annotation { "Feature Type Name" : "Feature", "Feature Type Description" : "" }
export const myFeature = defineFeature(function(context is Context, id is Id, definition is map)
    precondition{}
    {
        {
            var Q0;
            Q0=qCreatedBy(makeId("Front.planeOp"),FACE);
            var sketch = newSketch(context, id + "F0", { "sketchPlane" : qUnion([Q0])});
            skLineSegment(sketch, "E0.bottom", {"start": v(0, 0) * mm, "end": v(213.75, 0) * mm});
            skLineSegment(sketch, "E0.top", {"start": v(0, 261.75) * mm, "end": v(213.75, 261.75) * mm});
            skLineSegment(sketch, "E0.left", {"start": v(0, 0) * mm, "end": v(0, 261.75) * mm});
            skLineSegment(sketch, "E0.right", {"start": v(213.75, 0) * mm, "end": v(213.75, 261.75) * mm});
            skSolve(sketch);
        }
        {
            var Q0;
            Q0 = qSketchRegion(id + "F0", true);
            extrude(context, id + "F1", {"entities" : qUnion([Q0]), "oppositeDirection" : true, "depth" : 2 * mm, "offsetDistance" : 25 * mm});
        }
        {
            var Q0;
            Q0=qCreatedBy(makeId("Front.planeOp"),FACE);
            var sketch = newSketch(context, id + "F2", { "sketchPlane" : qUnion([Q0])});
            skCircle(sketch, "E1", {"center": v(41.2, 23.32) * mm, "radius": 8 * mm});
            skSolve(sketch);
        }
        {
            var Q0;
            Q0 = qSketchRegion(id + "F2", true);
            extrude(context, id + "F3", {"entities" : qUnion([Q0]), "operationType" : NewBodyOperationType.REMOVE, "oppositeDirection" : true, "depth" : 25 * mm, "offsetDistance" : 25 * mm});
        }
        {
            var Q0;
            Q0=makeQuery(id+"F1.opExtrude","CAP_FACE",FACE,{"disambiguationData":[OSD([sQuery(id+"F0.wireOp",EDGE,"E0.bottom"),sQuery(id+"F0.wireOp",EDGE,"E0.top"),sQuery(id+"F0.wireOp",EDGE,"E0.left"),sQuery(id+"F0.wireOp",EDGE,"E0.right")])],"isStart":true});
            var sketch = newSketch(context, id + "F4", { "sketchPlane" : qUnion([Q0])});
            skLineSegment(sketch, "E2.bottom", {"start": v(151.6, 32.62) * mm, "end": v(138.6, 32.62) * mm});
            skLineSegment(sketch, "E2.top", {"start": v(151.6, 14.02) * mm, "end": v(138.6, 14.02) * mm});
            skLineSegment(sketch, "E2.left", {"start": v(151.6, 32.62) * mm, "end": v(151.6, 14.02) * mm});
            skLineSegment(sketch, "E2.right", {"start": v(138.6, 32.62) * mm, "end": v(138.6, 14.02) * mm});
            skPoint(sketch, "E2.middle", {"position": v(145.1, 23.32) * mm});
            skSolve(sketch);
        }
        {
            var Q0;
            Q0 = qSketchRegion(id + "F4", true);
            extrude(context, id + "F5", {"entities" : qUnion([Q0]), "operationType" : NewBodyOperationType.REMOVE, "oppositeDirection" : true, "depth" : 25 * mm, "offsetDistance" : 25 * mm});
        }
        {
            var Q0;
            Q0=makeQuery(id+"F1.opExtrude","CAP_FACE",FACE,{"disambiguationData":[OSD([sQuery(id+"F0.wireOp",EDGE,"E0.bottom"),sQuery(id+"F0.wireOp",EDGE,"E0.top"),sQuery(id+"F0.wireOp",EDGE,"E0.left"),sQuery(id+"F0.wireOp",EDGE,"E0.right")])],"isStart":true});
            var sketch = newSketch(context, id + "F6", { "sketchPlane" : qUnion([Q0])});
            skText(sketch, "E3", { "text": "Emergency Stop", "fontName": "OpenSans-Regular.ttf"});
            const initialGuessF6  = {"E3": [0.058, 0.021, 1, 0, 0.005]};
            skSetInitialGuess(sketch, initialGuessF6);
            skSolve(sketch);
        }
        {
            var Q0;
            Q0 = qSketchRegion(id + "F6", true);
            extrude(context, id + "F7", {"entities" : qUnion([Q0]), "operationType" : NewBodyOperationType.REMOVE, "oppositeDirection" : true, "depth" : 0.5 * mm, "offsetDistance" : 25 * mm});
        }
        {
            var Q0;
            {var subQ0=sQuery(id+"F0.wireOp",EDGE,"E0.right");var subQ1=sQuery(id+"F0.wireOp",EDGE,"E0.left");var subQ2=sQuery(id+"F0.wireOp",EDGE,"E0.top");var subQ3=sQuery(id+"F0.wireOp",EDGE,"E0.bottom");Q0=makeQuery(id+"F7.boolean.opBoolean","SPLIT",FACE,{"disambiguationData":[TD([makeQuery(id+"F1.opExtrude","SWEPT_FACE",FACE,{"disambiguationData":[OSD([subQ3])]})])],"derivedFrom":makeQuery(id+"F1.opExtrude","CAP_FACE",FACE,{"disambiguationData":[OSD([subQ3,subQ2,subQ1,subQ0])],"isStart":true})});}
            var sketch = newSketch(context, id + "F8", { "sketchPlane" : qUnion([Q0])});
            skText(sketch, "E4", { "text": "Power", "fontName": "OpenSans-Bold.ttf"});
            const initialGuessF8  = {"E4": [0.157, 0.021, 1, 0, 0.00489]};
            skSetInitialGuess(sketch, initialGuessF8);
            skSolve(sketch);
        }
        {
            var Q0;
            Q0 = qSketchRegion(id + "F8", true);
            extrude(context, id + "F9", {"entities" : qUnion([Q0]), "operationType" : NewBodyOperationType.REMOVE, "oppositeDirection" : true, "depth" : 0.5 * mm, "offsetDistance" : 25 * mm});
        }
        {
            var Q0;
            {var subQ1=sQuery(id+"F0.wireOp",EDGE,"E0.bottom");var subQ2=makeQuery(id+"F1.opExtrude","SWEPT_FACE",FACE,{"disambiguationData":[OSD([subQ1])]});var subQ96=sQuery(id+"F0.wireOp",EDGE,"E0.right");var subQ100=sQuery(id+"F0.wireOp",EDGE,"E0.left");var subQ104=sQuery(id+"F0.wireOp",EDGE,"E0.top");Q0=makeQuery(id+"F9.boolean.opBoolean","SPLIT",FACE,{"disambiguationData":[TD([subQ2])],"derivedFrom":makeQuery(id+"F7.boolean.opBoolean","SPLIT",FACE,{"disambiguationData":[TD([subQ2])],"derivedFrom":makeQuery(id+"F1.opExtrude","CAP_FACE",FACE,{"disambiguationData":[OSD([subQ1,subQ104,subQ100,subQ96])],"isStart":true})})});}
            var sketch = newSketch(context, id + "F10", { "sketchPlane" : qUnion([Q0])});
            skCircle(sketch, "E5", {"center": v(41, 50) * mm, "radius": 1.35 * mm});
            skCircle(sketch, "E6", {"center": v(85, 50) * mm, "radius": 1.35 * mm});
            skCircle(sketch, "E7", {"center": v(129, 50) * mm, "radius": 1.35 * mm});
            skCircle(sketch, "E8", {"center": v(173, 50) * mm, "radius": 1.35 * mm});
            skCircle(sketch, "E9", {"center": v(41, 205.5) * mm, "radius": 1.35 * mm});
            skCircle(sketch, "E10", {"center": v(85, 205.5) * mm, "radius": 1.35 * mm});
            skCircle(sketch, "E11", {"center": v(129, 205.5) * mm, "radius": 1.35 * mm});
            skCircle(sketch, "E12", {"center": v(173, 205.5) * mm, "radius": 1.35 * mm});
            skCircle(sketch, "E13", {"center": v(11.88, 80) * mm, "radius": 1.35 * mm});
            skCircle(sketch, "E14", {"center": v(201.88, 80) * mm, "radius": 1.35 * mm});
            skCircle(sketch, "E15", {"center": v(201.88, 130) * mm, "radius": 1.35 * mm});
            skCircle(sketch, "E16", {"center": v(11.88, 130) * mm, "radius": 1.35 * mm});
            skCircle(sketch, "E17", {"center": v(11.88, 180) * mm, "radius": 1.35 * mm});
            skCircle(sketch, "E18", {"center": v(201.88, 180) * mm, "radius": 1.35 * mm});
            skSolve(sketch);
        }
        {
            var Q0;
            Q0 = qSketchRegion(id + "F10", true);
            extrude(context, id + "F11", {"entities" : qUnion([Q0]), "operationType" : NewBodyOperationType.REMOVE, "oppositeDirection" : true, "depth" : 25 * mm, "offsetDistance" : 25 * mm});
        }
        {
            var Q0;
            {var subQ1=sQuery(id+"F0.wireOp",EDGE,"E0.bottom");var subQ2=makeQuery(id+"F1.opExtrude","SWEPT_FACE",FACE,{"disambiguationData":[OSD([subQ1])]});var subQ96=sQuery(id+"F0.wireOp",EDGE,"E0.right");var subQ100=sQuery(id+"F0.wireOp",EDGE,"E0.left");var subQ104=sQuery(id+"F0.wireOp",EDGE,"E0.top");Q0=makeQuery(id+"F9.boolean.opBoolean","SPLIT",FACE,{"disambiguationData":[TD([subQ2])],"derivedFrom":makeQuery(id+"F7.boolean.opBoolean","SPLIT",FACE,{"disambiguationData":[TD([subQ2])],"derivedFrom":makeQuery(id+"F1.opExtrude","CAP_FACE",FACE,{"disambiguationData":[OSD([subQ1,subQ104,subQ100,subQ96])],"isStart":true})})});}
            var sketch = newSketch(context, id + "F12", { "sketchPlane" : qUnion([Q0])});
            skLineSegment(sketch, "E19.bottom", {"start": v(157.88, 75.5) * mm, "end": v(55.88, 75.5) * mm});
            skLineSegment(sketch, "E19.top", {"start": v(157.88, 54.5) * mm, "end": v(55.88, 54.5) * mm});
            skLineSegment(sketch, "E19.left", {"start": v(157.88, 75.5) * mm, "end": v(157.88, 54.5) * mm});
            skLineSegment(sketch, "E19.right", {"start": v(55.88, 75.5) * mm, "end": v(55.88, 54.5) * mm});
            skPoint(sketch, "E19.middle", {"position": v(106.88, 65) * mm});
            skSolve(sketch);
        }
        {
            var Q0;
            Q0 = qSketchRegion(id + "F12", true);
            extrude(context, id + "F13", {"entities" : qUnion([Q0]), "operationType" : NewBodyOperationType.REMOVE, "oppositeDirection" : true, "depth" : 25 * mm, "offsetDistance" : 25 * mm});
        }
        {
            var Q0;
            {var subQ1=sQuery(id+"F0.wireOp",EDGE,"E0.bottom");var subQ2=makeQuery(id+"F1.opExtrude","SWEPT_FACE",FACE,{"disambiguationData":[OSD([subQ1])]});var subQ96=sQuery(id+"F0.wireOp",EDGE,"E0.right");var subQ100=sQuery(id+"F0.wireOp",EDGE,"E0.left");var subQ104=sQuery(id+"F0.wireOp",EDGE,"E0.top");Q0=makeQuery(id+"F9.boolean.opBoolean","SPLIT",FACE,{"disambiguationData":[TD([subQ2])],"derivedFrom":makeQuery(id+"F7.boolean.opBoolean","SPLIT",FACE,{"disambiguationData":[TD([subQ2])],"derivedFrom":makeQuery(id+"F1.opExtrude","CAP_FACE",FACE,{"disambiguationData":[OSD([subQ1,subQ104,subQ100,subQ96])],"isStart":true})})});}
            var sketch = newSketch(context, id + "F14", { "sketchPlane" : qUnion([Q0])});
            skLineSegment(sketch, "E20.bottom", {"start": v(185.16, 186.15) * mm, "end": v(29.16, 186.15) * mm});
            skLineSegment(sketch, "E20.top", {"start": v(185.16, 98.15) * mm, "end": v(29.16, 98.15) * mm});
            skLineSegment(sketch, "E20.left", {"start": v(185.16, 186.15) * mm, "end": v(185.16, 98.15) * mm});
            skLineSegment(sketch, "E20.right", {"start": v(29.16, 186.15) * mm, "end": v(29.16, 98.15) * mm});
            skPoint(sketch, "E20.middle", {"position": v(107.16, 142.15) * mm});
            skSolve(sketch);
        }
        {
            var Q0;
            Q0 = qSketchRegion(id + "F14", true);
            extrude(context, id + "F15", {"entities" : qUnion([Q0]), "operationType" : NewBodyOperationType.REMOVE, "oppositeDirection" : true, "depth" : 25 * mm, "offsetDistance" : 25 * mm});
        }
        {
            var Q0;
            {var subQ1=sQuery(id+"F0.wireOp",EDGE,"E0.bottom");var subQ2=makeQuery(id+"F1.opExtrude","SWEPT_FACE",FACE,{"disambiguationData":[OSD([subQ1])]});var subQ96=sQuery(id+"F0.wireOp",EDGE,"E0.right");var subQ100=sQuery(id+"F0.wireOp",EDGE,"E0.left");var subQ104=sQuery(id+"F0.wireOp",EDGE,"E0.top");Q0=makeQuery(id+"F9.boolean.opBoolean","SPLIT",FACE,{"disambiguationData":[TD([subQ2])],"derivedFrom":makeQuery(id+"F7.boolean.opBoolean","SPLIT",FACE,{"disambiguationData":[TD([subQ2])],"derivedFrom":makeQuery(id+"F1.opExtrude","CAP_FACE",FACE,{"disambiguationData":[OSD([subQ1,subQ104,subQ100,subQ96])],"isStart":true})})});}
            var sketch = newSketch(context, id + "F16", { "sketchPlane" : qUnion([Q0])});
            skText(sketch, "E21", { "text": "Power Station 3p", "fontName": "OpenSans-Bold.ttf"});
            skText(sketch, "E22", { "text": "Realtime Control System", "fontName": "OpenSans-Regular.ttf"});
            const initialGuessF16  = {"E21": [0.08829, 0.24585, 1, 0, 0.0054], "E22": [0.08868, 0.23826, 1, 0, 0.00232]};
            skSetInitialGuess(sketch, initialGuessF16);
            skSolve(sketch);
        }
        {
            var Q0;
            Q0 = qSketchRegion(id + "F16", true);
            extrude(context, id + "F17", {"entities" : qUnion([Q0]), "operationType" : NewBodyOperationType.REMOVE, "oppositeDirection" : true, "depth" : 0.5 * mm, "offsetDistance" : 25 * mm});
        }
        {
            var Q0;
            {var subQ146=sQuery(id+"F0.wireOp",EDGE,"E0.right");var subQ148=sQuery(id+"F0.wireOp",EDGE,"E0.left");var subQ150=sQuery(id+"F0.wireOp",EDGE,"E0.bottom");var subQ151=makeQuery(id+"F1.opExtrude","SWEPT_FACE",FACE,{"disambiguationData":[OSD([subQ150])]});var subQ189=sQuery(id+"F0.wireOp",EDGE,"E0.top");Q0=makeQuery(id+"F17.boolean.opBoolean","SPLIT",FACE,{"disambiguationData":[TD([subQ151])],"derivedFrom":makeQuery(id+"F9.boolean.opBoolean","SPLIT",FACE,{"disambiguationData":[TD([subQ151])],"derivedFrom":makeQuery(id+"F7.boolean.opBoolean","SPLIT",FACE,{"disambiguationData":[TD([subQ151])],"derivedFrom":makeQuery(id+"F1.opExtrude","CAP_FACE",FACE,{"disambiguationData":[OSD([subQ150,subQ189,subQ148,subQ146])],"isStart":true})})})});}
            var sketch = newSketch(context, id + "F18", { "sketchPlane" : qUnion([Q0])});
            skLineSegment(sketch, "E23.bottom", {"start": v(10.5, 4.75) * mm, "end": v(4.4, 4.75) * mm});
            skLineSegment(sketch, "E23.top", {"start": v(10.5, 1.25) * mm, "end": v(4.4, 1.25) * mm});
            skLineSegment(sketch, "E23.left", {"start": v(10.5, 4.75) * mm, "end": v(10.5, 1.25) * mm});
            skLineSegment(sketch, "E23.right", {"start": v(4.4, 4.75) * mm, "end": v(4.4, 1.25) * mm});
            skPoint(sketch, "E23.middle", {"position": v(7.45, 3) * mm});
            skLineSegment(sketch, "E24.bottom", {"start": v(209.5, 4.75) * mm, "end": v(203.4, 4.75) * mm});
            skLineSegment(sketch, "E24.top", {"start": v(209.5, 1.25) * mm, "end": v(203.4, 1.25) * mm});
            skLineSegment(sketch, "E24.left", {"start": v(209.5, 4.75) * mm, "end": v(209.5, 1.25) * mm});
            skLineSegment(sketch, "E24.right", {"start": v(203.4, 4.75) * mm, "end": v(203.4, 1.25) * mm});
            skPoint(sketch, "E24.middle", {"position": v(206.45, 3) * mm});
            skLineSegment(sketch, "E25.bottom", {"start": v(209.5, 260.5) * mm, "end": v(203.4, 260.5) * mm});
            skLineSegment(sketch, "E25.top", {"start": v(209.5, 257) * mm, "end": v(203.4, 257) * mm});
            skLineSegment(sketch, "E25.left", {"start": v(209.5, 260.5) * mm, "end": v(209.5, 257) * mm});
            skLineSegment(sketch, "E25.right", {"start": v(203.4, 260.5) * mm, "end": v(203.4, 257) * mm});
            skPoint(sketch, "E25.middle", {"position": v(206.45, 258.75) * mm});
            skPoint(sketch, "E25.middle.positionSnap0", {"position": v(206.45, 4.75) * mm});
            skPoint(sketch, "E25.centerSnap0", {"position": v(206.45, 4.75) * mm});
            skLineSegment(sketch, "E26.bottom", {"start": v(10.5, 260.5) * mm, "end": v(4.4, 260.5) * mm});
            skLineSegment(sketch, "E26.top", {"start": v(10.5, 257) * mm, "end": v(4.4, 257) * mm});
            skLineSegment(sketch, "E26.left", {"start": v(10.5, 260.5) * mm, "end": v(10.5, 257) * mm});
            skLineSegment(sketch, "E26.right", {"start": v(4.4, 260.5) * mm, "end": v(4.4, 257) * mm});
            skPoint(sketch, "E26.middle", {"position": v(7.45, 258.75) * mm});
            skSolve(sketch);
        }
        {
            var Q0;
            Q0 = qSketchRegion(id + "F18", true);
            extrude(context, id + "F19", {"entities" : qUnion([Q0]), "operationType" : NewBodyOperationType.REMOVE, "oppositeDirection" : true, "depth" : 25 * mm, "offsetDistance" : 25 * mm});
        }
        {
            var Q0;
            {var subQ146=sQuery(id+"F0.wireOp",EDGE,"E0.right");var subQ148=sQuery(id+"F0.wireOp",EDGE,"E0.left");var subQ150=sQuery(id+"F0.wireOp",EDGE,"E0.bottom");var subQ151=makeQuery(id+"F1.opExtrude","SWEPT_FACE",FACE,{"disambiguationData":[OSD([subQ150])]});var subQ189=sQuery(id+"F0.wireOp",EDGE,"E0.top");Q0=makeQuery(id+"F17.boolean.opBoolean","SPLIT",FACE,{"disambiguationData":[TD([subQ151])],"derivedFrom":makeQuery(id+"F9.boolean.opBoolean","SPLIT",FACE,{"disambiguationData":[TD([subQ151])],"derivedFrom":makeQuery(id+"F7.boolean.opBoolean","SPLIT",FACE,{"disambiguationData":[TD([subQ151])],"derivedFrom":makeQuery(id+"F1.opExtrude","CAP_FACE",FACE,{"disambiguationData":[OSD([subQ150,subQ189,subQ148,subQ146])],"isStart":true})})})});}
            var sketch = newSketch(context, id + "F20", { "sketchPlane" : qUnion([Q0])});
            skLineSegment(sketch, "E27.bottom", {"start": v(191.7, 188.62) * mm, "end": v(27.2, 188.62) * mm});
            skLineSegment(sketch, "E27.top", {"start": v(191.7, 91.12) * mm, "end": v(27.2, 91.12) * mm});
            skLineSegment(sketch, "E27.left", {"start": v(191.7, 188.62) * mm, "end": v(191.7, 91.12) * mm});
            skLineSegment(sketch, "E27.right", {"start": v(27.2, 188.62) * mm, "end": v(27.2, 91.12) * mm});
            skPoint(sketch, "E27.middle", {"position": v(109.45, 139.87) * mm});
            skSolve(sketch);
        }
        {
            var Q0;
            Q0 = qSketchRegion(id + "F20", true);
            extrude(context, id + "F21", {"entities" : qUnion([Q0]), "operationType" : NewBodyOperationType.REMOVE, "oppositeDirection" : true, "depth" : 1 * mm, "offsetDistance" : 25 * mm});
        }
        {
            var Q0;
            Q0=makeQuery(id+"F21.boolean.opBoolean","COPY",FACE,{"derivedFrom":makeQuery(id+"F21.opExtrude","CAP_FACE",FACE,{"disambiguationData":[OSD([sQuery(id+"F20.wireOp",EDGE,"E27.bottom"),sQuery(id+"F20.wireOp",EDGE,"E27.top"),sQuery(id+"F20.wireOp",EDGE,"E27.left"),sQuery(id+"F20.wireOp",EDGE,"E27.right")])],"isStart":false})});
            var sketch = newSketch(context, id + "F22", { "sketchPlane" : qUnion([Q0])});
            skLineSegment(sketch, "E28.bottom", {"start": v(156.7, 105.02) * mm, "end": v(121.7, 105.02) * mm});
            skLineSegment(sketch, "E28.top", {"start": v(156.7, 93.85) * mm, "end": v(121.7, 93.85) * mm});
            skLineSegment(sketch, "E28.left", {"start": v(156.7, 105.02) * mm, "end": v(156.7, 93.85) * mm});
            skLineSegment(sketch, "E28.right", {"start": v(121.7, 105.02) * mm, "end": v(121.7, 93.85) * mm});
            skSolve(sketch);
        }
        {
            var Q0;
            Q0 = qSketchRegion(id + "F22", true);
            extrude(context, id + "F23", {"entities" : qUnion([Q0]), "operationType" : NewBodyOperationType.REMOVE, "oppositeDirection" : true, "depth" : 25 * mm, "offsetDistance" : 25 * mm});
        }
    });